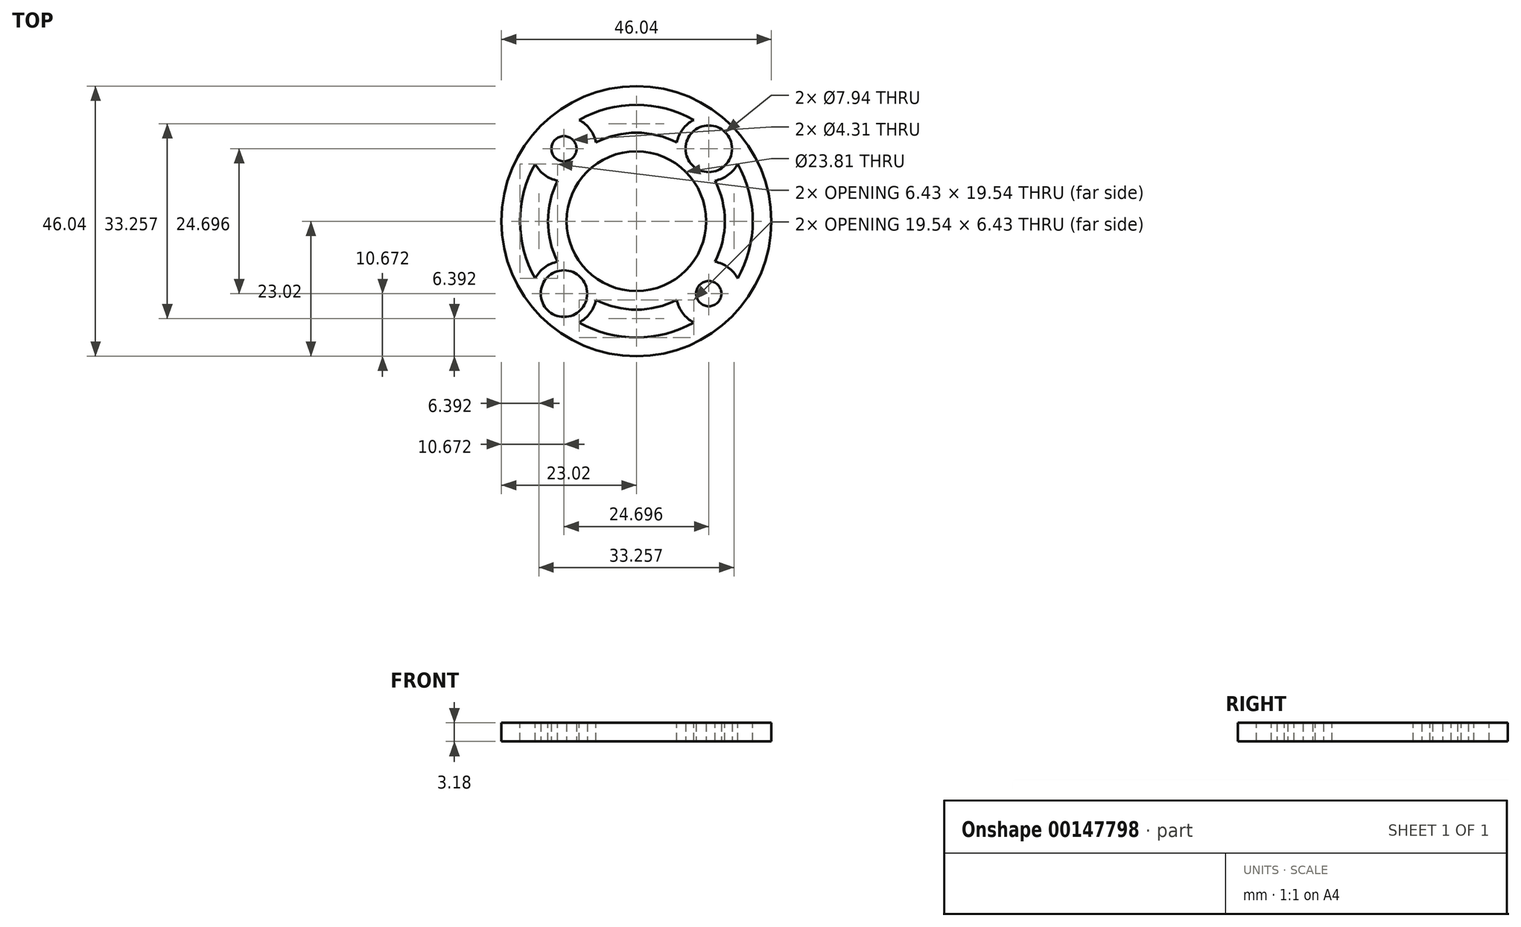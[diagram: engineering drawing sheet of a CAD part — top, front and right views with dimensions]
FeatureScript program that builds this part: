
annotation { "Feature Type Name" : "Feature", "Feature Type Description" : "" }
export const myFeature = defineFeature(function(context is Context, id is Id, definition is map)
    precondition{}
    {
        {
            var Q0;
            Q0=qCreatedBy(makeId("Top.planeOp"),FACE);
            var sketch = newSketch(context, id + "F0", { "sketchPlane" : qUnion([Q0])});
            skCircle(sketch, "E0", {"center": v(0, 0) * mm, "radius": 23.02 * mm});
            skCircle(sketch, "E1", {"center": v(0, 0) * mm, "radius": 11.9 * mm});
            skLineSegment(sketch, "E2.bottom", {"start": v(-12.35, 12.35) * mm, "end": v(12.35, 12.35) * mm, "construction": true});
            skLineSegment(sketch, "E2.top", {"start": v(-12.35, -12.35) * mm, "end": v(12.35, -12.35) * mm, "construction": true});
            skLineSegment(sketch, "E2.left", {"start": v(-12.35, 12.35) * mm, "end": v(-12.35, -12.35) * mm, "construction": true});
            skLineSegment(sketch, "E2.right", {"start": v(12.35, 12.35) * mm, "end": v(12.35, -12.35) * mm, "construction": true});
            skCircle(sketch, "E3", {"center": v(-12.35, 12.35) * mm, "radius": 5.56 * mm, "construction": true});
            skCircle(sketch, "E4", {"center": v(12.35, 12.35) * mm, "radius": 3.97 * mm});
            skCircle(sketch, "E5", {"center": v(-12.35, 12.35) * mm, "radius": 2.15 * mm});
            skCircle(sketch, "E6", {"center": v(-12.35, -12.35) * mm, "radius": 3.97 * mm});
            skCircle(sketch, "E7", {"center": v(12.35, -12.35) * mm, "radius": 2.15 * mm});
            skSolve(sketch);
        }
        {
            var Q0;
            Q0=qSketchRegion(id+"F0",true);
            extrude(context, id + "F1", {"entities" : qUnion([Q0]), "depth" : 3.17 * mm});
        }
        {
            var Q0;
            Q0=makeQuery(id+"F1.opExtrude","CAP_FACE",FACE,{"disambiguationData":[OSD([sQuery(id+"F0.wireOp",EDGE,"E0"),sQuery(id+"F0.wireOp",EDGE,"E1"),sQuery(id+"F0.wireOp",EDGE,"E4"),sQuery(id+"F0.wireOp",EDGE,"E5"),sQuery(id+"F0.wireOp",EDGE,"E6"),sQuery(id+"F0.wireOp",EDGE,"E7")])],"isStart":false});
            var sketch = newSketch(context, id + "F2", { "sketchPlane" : qUnion([Q0])});
            skArc(sketch, "E8", {"start": v(-6.9, 13.41) * mm, "mid": v(-7.9, 15.67) * mm, "end": v(-9.77, 17.27) * mm});
            skArc(sketch, "E9", {"start": v(9.77, 17.27) * mm, "mid": v(7.9, 15.67) * mm, "end": v(6.9, 13.41) * mm});
            skArc(sketch, "E10", {"start": v(6.9, 13.41) * mm, "mid": v(0, 15.08) * mm, "end": v(-6.9, 13.41) * mm});
            skArc(sketch, "E11", {"start": v(9.77, 17.27) * mm, "mid": v(0, 19.84) * mm, "end": v(-9.77, 17.27) * mm});
            skArc(sketch, "E12", {"start": v(-17.27, 9.77) * mm, "mid": v(-15.67, 7.9) * mm, "end": v(-13.41, 6.9) * mm});
            skArc(sketch, "E13", {"start": v(-13.41, 6.9) * mm, "mid": v(-15.08, 0) * mm, "end": v(-13.41, -6.9) * mm});
            skArc(sketch, "E14", {"start": v(-13.41, -6.9) * mm, "mid": v(-15.67, -7.9) * mm, "end": v(-17.27, -9.77) * mm});
            skArc(sketch, "E15", {"start": v(-17.27, 9.77) * mm, "mid": v(-19.84, 0) * mm, "end": v(-17.27, -9.77) * mm});
            skArc(sketch, "E16", {"start": v(13.41, 6.9) * mm, "mid": v(15.67, 7.9) * mm, "end": v(17.27, 9.77) * mm});
            skArc(sketch, "E17", {"start": v(17.27, -9.77) * mm, "mid": v(19.84, 0) * mm, "end": v(17.27, 9.77) * mm});
            skArc(sketch, "E18", {"start": v(13.41, -6.9) * mm, "mid": v(15.08, 0) * mm, "end": v(13.41, 6.9) * mm});
            skArc(sketch, "E19", {"start": v(17.27, -9.77) * mm, "mid": v(15.67, -7.9) * mm, "end": v(13.41, -6.9) * mm});
            skArc(sketch, "E20", {"start": v(-9.77, -17.27) * mm, "mid": v(-7.9, -15.67) * mm, "end": v(-6.9, -13.41) * mm});
            skArc(sketch, "E21", {"start": v(6.9, -13.41) * mm, "mid": v(7.9, -15.67) * mm, "end": v(9.77, -17.27) * mm});
            skArc(sketch, "E22", {"start": v(-6.9, -13.41) * mm, "mid": v(0, -15.08) * mm, "end": v(6.9, -13.41) * mm});
            skArc(sketch, "E23", {"start": v(-9.77, -17.27) * mm, "mid": v(0, -19.84) * mm, "end": v(9.77, -17.27) * mm});
            skSolve(sketch);
        }
        {
            var Q0;
            Q0=qSketchRegion(id+"F2",true);
            var Q1;
            Q1=makeQuery(id+"F1.opExtrude","CAP_FACE",FACE,{"disambiguationData":[OSD([sQuery(id+"F0.wireOp",EDGE,"E0"),sQuery(id+"F0.wireOp",EDGE,"E1"),sQuery(id+"F0.wireOp",EDGE,"E4"),sQuery(id+"F0.wireOp",EDGE,"E5"),sQuery(id+"F0.wireOp",EDGE,"E6"),sQuery(id+"F0.wireOp",EDGE,"E7")])],"isStart":true});
            extrude(context, id + "F3", {"entities" : qUnion([Q0]), "operationType" : NewBodyOperationType.REMOVE, "endBound" : BoundingType.UP_TO_SURFACE, "oppositeDirection" : true, "endBoundEntityFace" : qUnion([Q1]), "depth" : 25.4 * mm});
        }
    });
